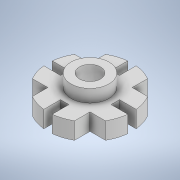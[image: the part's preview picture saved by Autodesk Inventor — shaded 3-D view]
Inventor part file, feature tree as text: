
AUTODESK INVENTOR PART (.ipt)
format: ipt  version: 2022.2 (Build 262287030, 287C)  size: 160,256 bytes
history: native  units: in
note: dims shown in document units (in); Inventor stores cm internally (conversion verified against a paired STEP export)
features: sketch x4, extrude x3, hole x1
ambient origin geometry x8: Origin, YZ Plane, XZ Plane, XY Plane, X Axis, Y Axis, Z Axis, Center Point
bodies: Solid1 (feature_tree)
feature tree (8):
  extrude  "Extrusion1"  Depth=1.0in TaperAngle=0.0deg
  extrude  "Extrusion2"  Depth=0.75in TaperAngle=0.0deg
  hole  "Hole1"  [1 undecoded]
  extrude  "Extrusion3"  Depth=2.5in
  sketch  "Sketch1"  dims[d0=5.0in d1=1.0in d2=0.0in]
  sketch  "Sketch2"  dims[d3=2.25in d4=0.75in d5=0.0in]
  sketch  "Sketch3"  dims[d6=1.25in d7=0.75in d8=2.0in d9=0.125in d10=0.5635in d11=1.0in d12=0.8108in d13=0.5in]
  sketch  "Sketch4"  dims[d14=3.0in d15=2.5in d16=2.5in d17=1.5748in d19=360.0deg d21=0.0in d22=0.0in]
note: 1 required parameter value undecoded (feature->parameter linkage not recoverable at this tier; creation-order binding heuristic only, values carry confidence <= 0.55)
